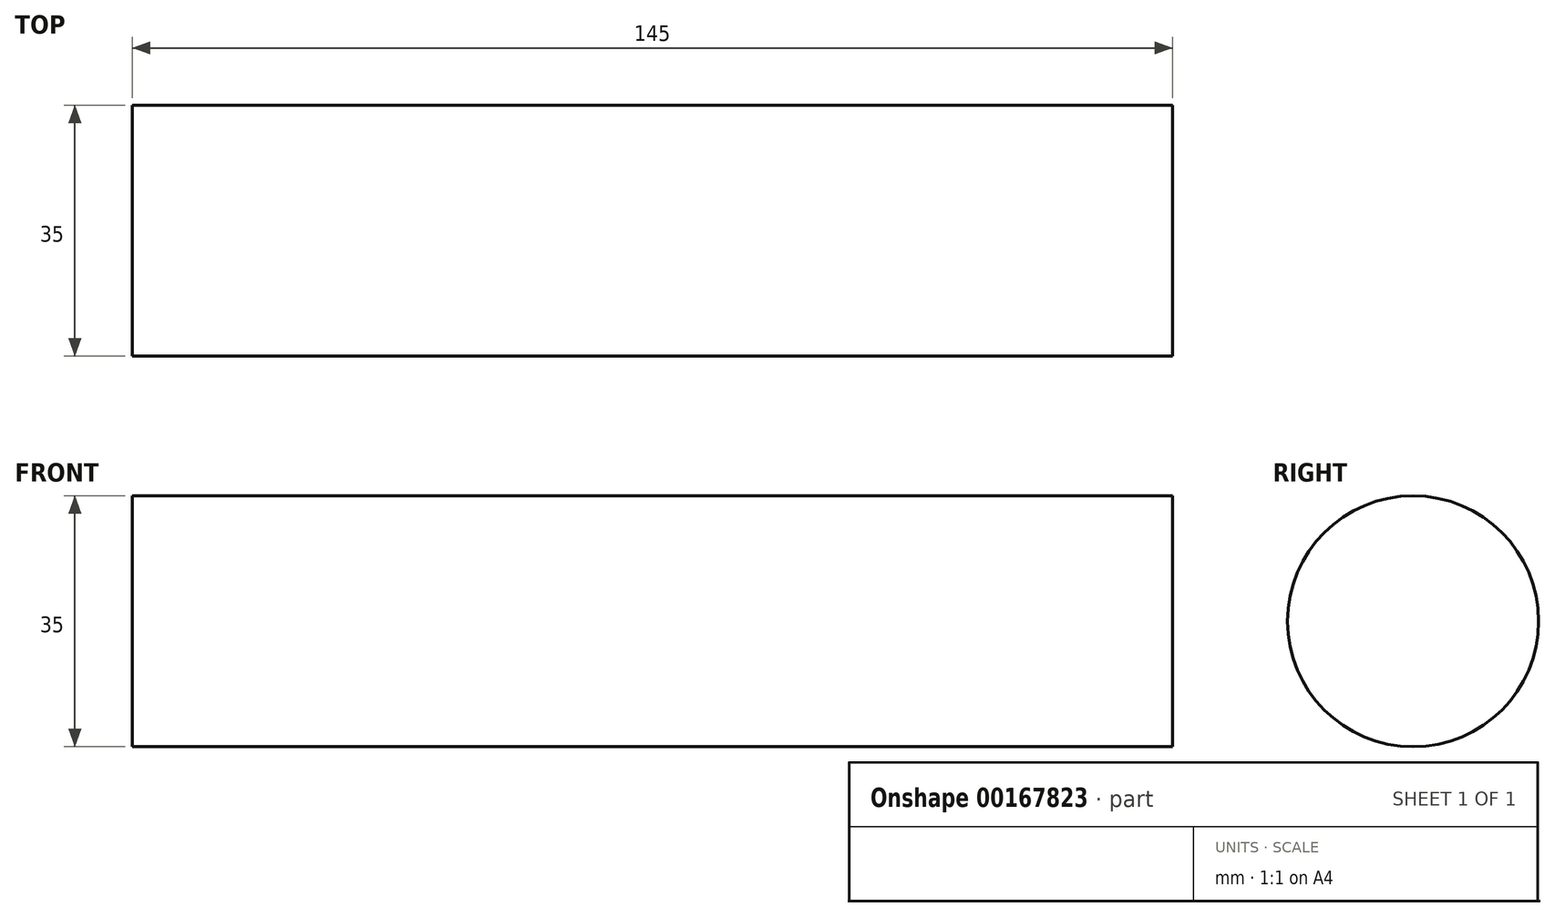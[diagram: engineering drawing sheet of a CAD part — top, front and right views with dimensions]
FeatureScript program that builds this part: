
annotation { "Feature Type Name" : "Feature", "Feature Type Description" : "" }
export const myFeature = defineFeature(function(context is Context, id is Id, definition is map)
    precondition{}
    {
        {
            var Q0;
            Q0=qCreatedBy(makeId("Right.planeOp"),FACE);
            var sketch = newSketch(context, id + "F0", { "sketchPlane" : qUnion([Q0])});
            skCircle(sketch, "E0", {"center": v(0, 0) * mm, "radius": 17.5 * mm});
            skSolve(sketch);
        }
        {
            var Q0;
            Q0=makeQuery(id+"F0.imprint","IMPRINT",FACE,{"disambiguationData":[TD([[makeQuery(id+"F0.imprint","IMPRINT",EDGE,{"derivedFrom":sQuery(id+"F0.wireOp",EDGE,"E0")}),1.0]])]});
            extrude(context, id + "F1", {"entities" : qUnion([Q0]), "depth" : 145 * mm});
        }
    });
